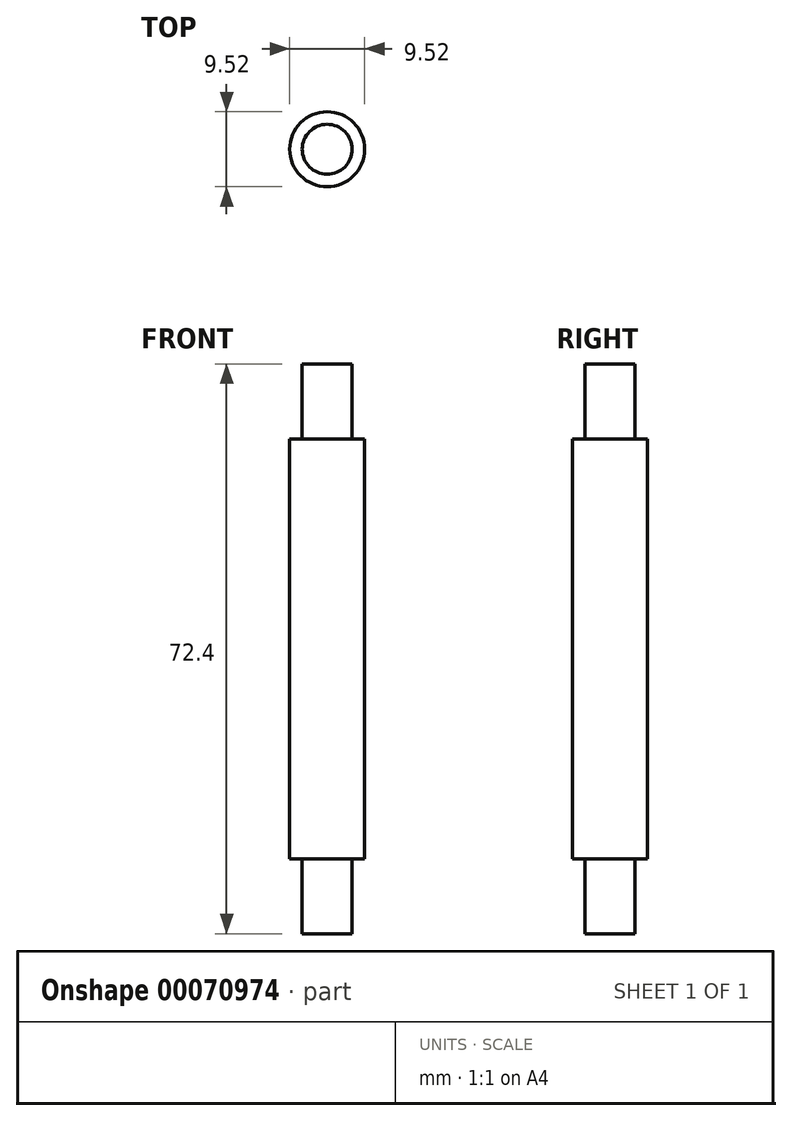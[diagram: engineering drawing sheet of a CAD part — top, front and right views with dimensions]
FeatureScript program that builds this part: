
annotation { "Feature Type Name" : "Feature", "Feature Type Description" : "" }
export const myFeature = defineFeature(function(context is Context, id is Id, definition is map)
    precondition{}
    {
        {
            var Q0;
            Q0=qCreatedBy(makeId("Top.planeOp"),FACE);
            var sketch = newSketch(context, id + "F0", { "sketchPlane" : qUnion([Q0])});
            skCircle(sketch, "E0", {"center": v(0, 0) * mm, "radius": 4.76 * mm});
            skSolve(sketch);
        }
        {
            var Q0;
            Q0=qSketchRegion(id+"F0",true);
            extrude(context, id + "F1", {"entities" : qUnion([Q0]), "depth" : 53.34 * mm});
        }
        {
            var Q0;
            Q0=makeQuery(id+"F1.opExtrude","CAP_FACE",FACE,{"disambiguationData":[OSD([sQuery(id+"F0.wireOp",EDGE,"E0")])],"isStart":false});
            var sketch = newSketch(context, id + "F2", { "sketchPlane" : qUnion([Q0])});
            skCircle(sketch, "E1", {"center": v(0, 0) * mm, "radius": 3.18 * mm});
            skSolve(sketch);
        }
        {
            var Q0;
            Q0=qSketchRegion(id+"F2",true);
            extrude(context, id + "F3", {"entities" : qUnion([Q0]), "operationType" : NewBodyOperationType.ADD, "depth" : 9.52 * mm});
        }
        {
            var Q0;
            Q0=makeQuery(id+"F1.opExtrude","CAP_FACE",FACE,{"disambiguationData":[OSD([sQuery(id+"F0.wireOp",EDGE,"E0")])],"isStart":true});
            var sketch = newSketch(context, id + "F4", { "sketchPlane" : qUnion([Q0])});
            skCircle(sketch, "E2", {"center": v(0, 0) * mm, "radius": 3.18 * mm});
            skSolve(sketch);
        }
        {
            var Q0;
            Q0=qSketchRegion(id+"F4",true);
            extrude(context, id + "F5", {"entities" : qUnion([Q0]), "operationType" : NewBodyOperationType.ADD, "depth" : 9.52 * mm});
        }
    });
